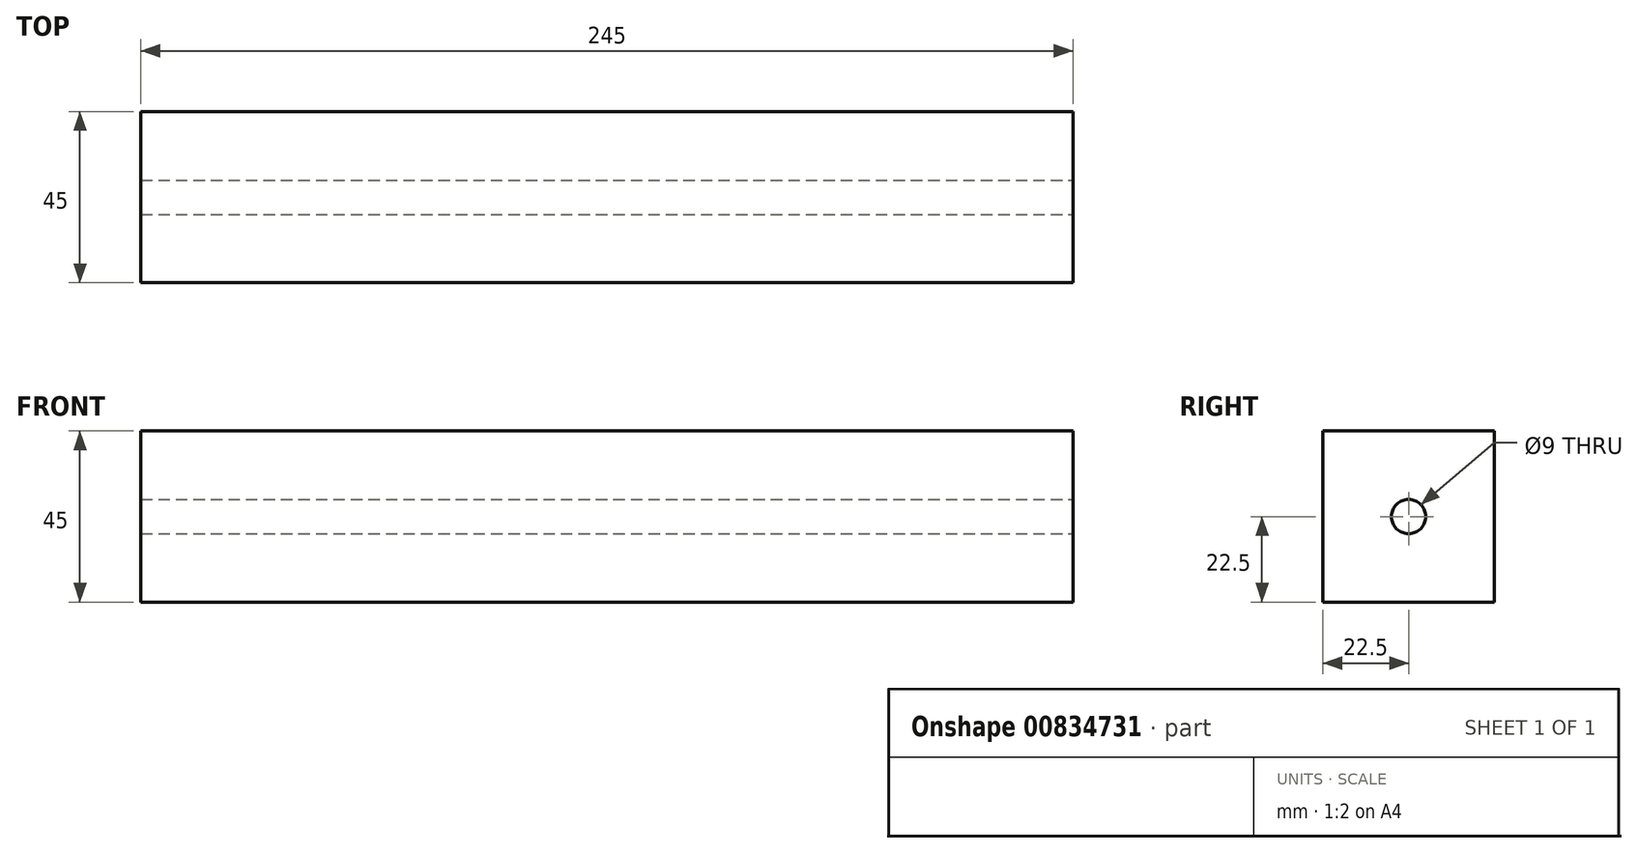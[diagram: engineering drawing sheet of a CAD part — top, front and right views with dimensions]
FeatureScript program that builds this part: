
annotation { "Feature Type Name" : "Feature", "Feature Type Description" : "" }
export const myFeature = defineFeature(function(context is Context, id is Id, definition is map)
    precondition{}
    {
        {
            var Q0;
            Q0=qCreatedBy(makeId("Right.planeOp"),FACE);
            var sketch = newSketch(context, id + "F0", { "sketchPlane" : qUnion([Q0])});
            skLineSegment(sketch, "E0.bottom", {"start": v(-22.5, 22.5) * mm, "end": v(22.5, 22.5) * mm});
            skLineSegment(sketch, "E0.top", {"start": v(-22.5, -22.5) * mm, "end": v(22.5, -22.5) * mm});
            skLineSegment(sketch, "E0.left", {"start": v(-22.5, 22.5) * mm, "end": v(-22.5, -22.5) * mm});
            skLineSegment(sketch, "E0.right", {"start": v(22.5, 22.5) * mm, "end": v(22.5, -22.5) * mm});
            skPoint(sketch, "E0.middle", {"position": v(0, 0) * mm});
            skCircle(sketch, "E1", {"center": v(0, 0) * mm, "radius": 4.5 * mm});
            skSolve(sketch);
        }
        {
            var Q0;
            Q0=makeQuery(id+"F0.imprint","IMPRINT",FACE,{"disambiguationData":[TD([[makeQuery(id+"F0.imprint","IMPRINT",EDGE,{"derivedFrom":sQuery(id+"F0.wireOp",EDGE,"E0.bottom")}),-1.0]])]});
            extrude(context, id + "F1", {"entities" : qUnion([Q0]), "oppositeDirection" : true, "depth" : 245 * mm, "offsetDistance" : 25 * mm});
        }
    });
